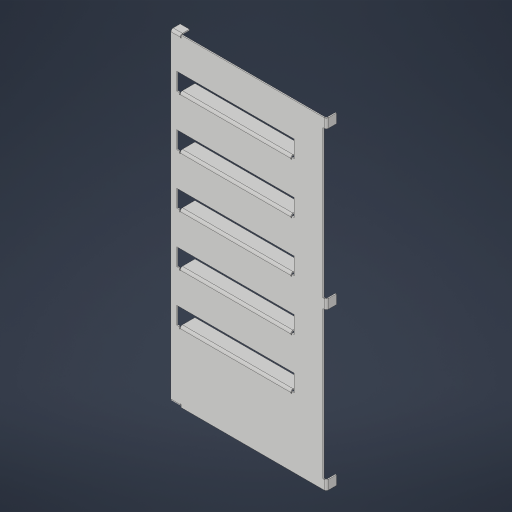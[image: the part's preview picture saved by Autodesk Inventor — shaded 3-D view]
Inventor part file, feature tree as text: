
AUTODESK INVENTOR PART (.ipt)
format: ipt  version: 2023.4 (Build 274418000, 418)  size: 449,024 bytes
history: native  units: in
note: dims shown in document units (in); Inventor stores cm internally (conversion verified against a paired STEP export)
features: sheet_metal_op x12, sketch x7, other x5, extrude x2, projected_geometry x2, pattern_linear x1
ambient origin geometry x8: Origin, YZ Plane, XZ Plane, XY Plane, X Axis, Y Axis, Z Axis, Center Point
bodies: Solid1 (feature_tree)
feature tree (29):
  sheet_metal_op  "Face1"
  sketch  "Sketch2"  dims[d1=35.0in]
  sheet_metal_op  "Face2"
  sheet_metal_op  "Fold1"
  sheet_metal_op  "Fold2"
  sketch  "Sketch3"  dims[d2=0.12in]
  sheet_metal_op  "Fold4"
  pattern_linear  "Rectangular Pattern1"  Spacing1=1.0in  [1 undecoded]
  extrude  "Extrusion1"  Depth=1.5in
  sheet_metal_op  "Flange1"
  sheet_metal_op  "Flange2"
  extrude  "Extrusion2"  Depth=1.0in
  sketch  "Sketch1"  dims[d0=16.5in]
  other  "Plate1"
  other  "Plate2"
  sheet_metal_op  "Bend1"
  sketch  "Sketch4"  dims[d3=1.25in]
  sketch  "Sketch5"  dims[d4=1.0in]
  other  "Plate3"
  sheet_metal_op  "Bend2"
  sheet_metal_op  "Corner1"
  sketch  "Sketch6"  dims[d5=0.25in]
  other  "Plate4"
  sheet_metal_op  "Bend3"
  sheet_metal_op  "Corner2"
  sketch  "Sketch7"  dims[d6=1.0in d7=1.0in d8=1.25in d9=1.0in d10=0.25in d11=0.12in d12=0.12in d13=0.06in d14=0.24in d15=0.12in d16=0.12in d17=0.06in d18=0.24in d19=0.12in d20=90.0deg d21=0.12in d22=0.12in d23=0.06in d24=0.24in d25=0.12in d26=90.0deg d27=0.12in d28=5.5in d29=1.5in d30=12.0in d31=1.0in d32=0.375in d33=0.12in d34=0.0in d41=0.12in d42=0.06in d43=0.24in d44=0.12in d45=90.0deg d46=0.12in d47=1.9685in d49=5.5in d50=1.0in d51=0.0in d52=0.12in d53=0.06in d54=0.24in d55=0.12in d56=1.0in d57=0.0in d58=1.0in d59=90.0deg d60=0.12in d61=0.48in d62=0.12in d63=0.12in d64=0.12in d65=0.06in d66=0.24in d67=0.12in d68=1.0in d69=0.0in d70=1.0in d71=90.0deg d72=0.12in d73=0.48in d74=0.12in d75=0.12in d76=11.31in d77=1.5in d78=4.45in d79=1.5in d80=5.35in d81=4.45in d82=0.0in d83=0.0in]
  other  "Cut1"
  projected_geometry  "Project Cut Edges1"
  projected_geometry  "Project Cut Edges2"
note: 1 required parameter value undecoded (feature->parameter linkage not recoverable at this tier; creation-order binding heuristic only, values carry confidence <= 0.55)
